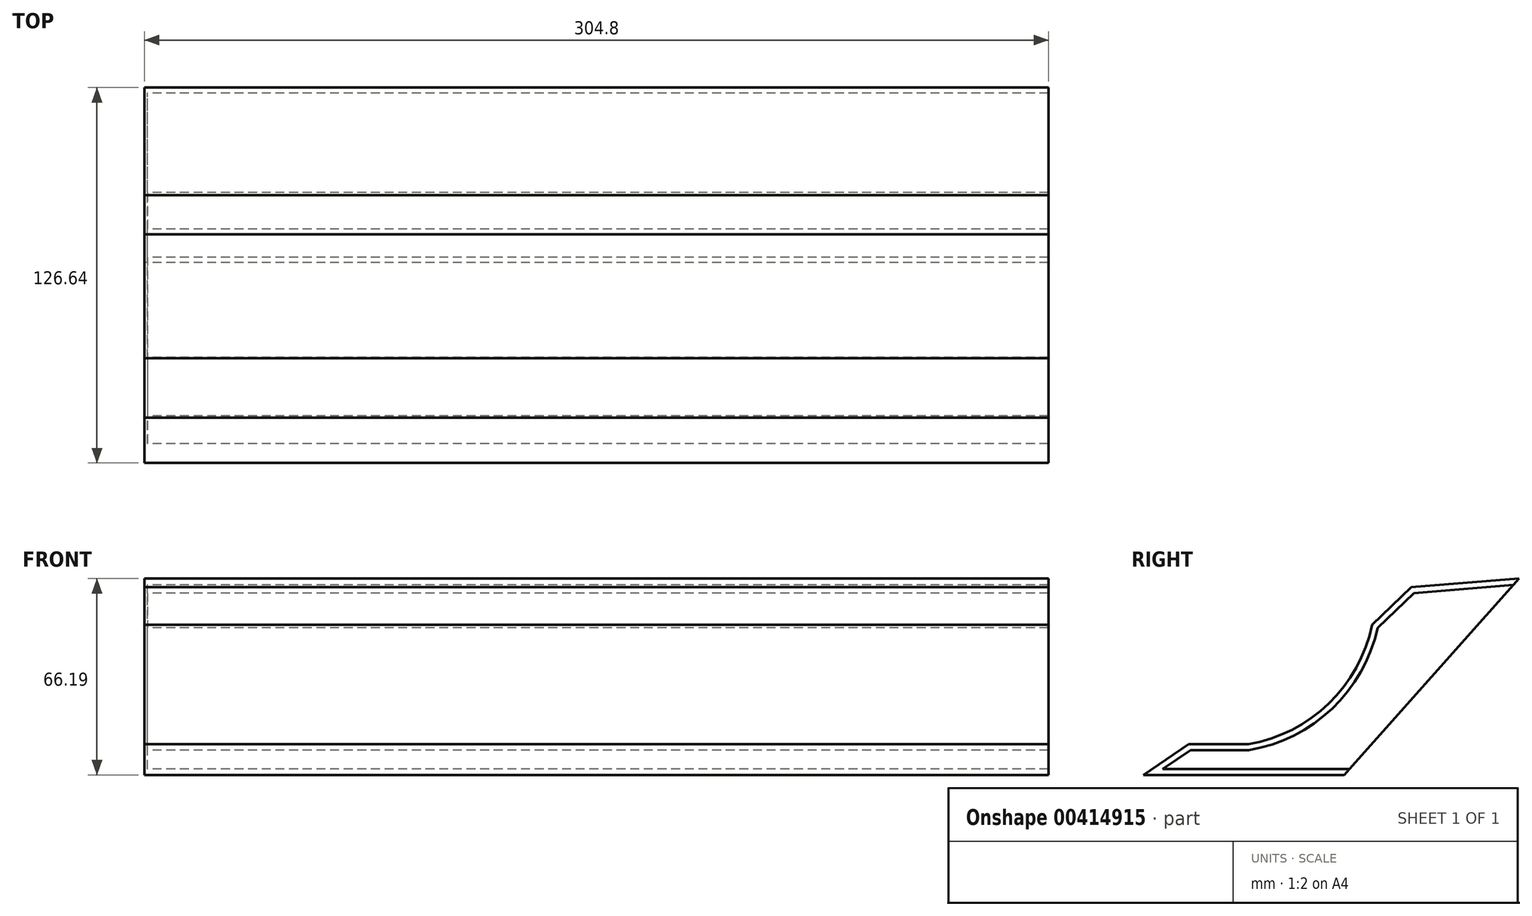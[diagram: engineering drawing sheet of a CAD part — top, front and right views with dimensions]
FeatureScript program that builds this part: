
annotation { "Feature Type Name" : "Feature", "Feature Type Description" : "" }
export const myFeature = defineFeature(function(context is Context, id is Id, definition is map)
    precondition{}
    {
        {
            var Q0;
            Q0=qCreatedBy(makeId("Right.planeOp"),FACE);
            var sketch = newSketch(context, id + "F0", { "sketchPlane" : qUnion([Q0])});
            skArc(sketch, "E0", {"start": v(-54.97, 0) * mm, "mid": v(-27.89, 13.7) * mm, "end": v(-13.24, 40.3) * mm});
            skLineSegment(sketch, "E1", {"start": v(-13.24, 40.3) * mm, "end": v(0, 52.93) * mm});
            skLineSegment(sketch, "E2", {"start": v(-22.72, -10.36) * mm, "end": v(36.26, 55.83) * mm});
            skLineSegment(sketch, "E3", {"start": v(-75.12, 0) * mm, "end": v(-54.97, 0) * mm});
            skLineSegment(sketch, "E4", {"start": v(36.26, 55.83) * mm, "end": v(0, 52.93) * mm});
            skLineSegment(sketch, "E5", {"start": v(-75.12, 0) * mm, "end": v(-90.38, -10.36) * mm});
            skPoint(sketch, "E6.orphan", {"position": v(-75.58, -10.36) * mm});
            skPoint(sketch, "E7.start.orphan", {"position": v(-77.31, -10.36) * mm});
            skLineSegment(sketch, "E8", {"start": v(-90.38, -10.36) * mm, "end": v(-22.72, -10.36) * mm});
            skSolve(sketch);
        }
        {
            var Q0;
            Q0=makeQuery(id+"F0.imprint","IMPRINT",FACE,{"disambiguationData":[TD([[makeQuery(id+"F0.imprint","IMPRINT",EDGE,{"derivedFrom":sQuery(id+"F0.wireOp",EDGE,"E0")}),-1.0]])]});
            extrude(context, id + "F1", {"entities" : qUnion([Q0]), "depth" : 1 * mm});
        }
        {
            var Q0;
            Q0=makeQuery(id+"F0.imprint","IMPRINT",FACE,{"disambiguationData":[TD([[makeQuery(id+"F0.imprint","IMPRINT",EDGE,{"derivedFrom":sQuery(id+"F0.wireOp",EDGE,"E0")}),-1.0]])]});
            var sketch = newSketch(context, id + "F2", { "sketchPlane" : qUnion([Q0])});
            skLineSegment(sketch, "E9.0", {"start": v(-74.5, -2) * mm, "end": v(-54.8, -2) * mm});
            skArc(sketch, "E9.1", {"start": v(-54.8, -2) * mm, "mid": v(-26.79, 12) * mm, "end": v(-11.41, 39.27) * mm});
            skLineSegment(sketch, "E9.2", {"start": v(-11.41, 39.27) * mm, "end": v(0.87, 51) * mm});
            skLineSegment(sketch, "E9.3", {"start": v(34.34, 53.67) * mm, "end": v(0.87, 51) * mm});
            skLineSegment(sketch, "E10.0", {"start": v(-83.87, -8.36) * mm, "end": v(-20.94, -8.36) * mm});
            skLineSegment(sketch, "E10.1", {"start": v(-74.5, -2) * mm, "end": v(-83.87, -8.36) * mm});
            skLineSegment(sketch, "E11.0", {"start": v(-90.38, -10.36) * mm, "end": v(-22.72, -10.36) * mm});
            skLineSegment(sketch, "E11.1", {"start": v(-75.12, 0) * mm, "end": v(-90.38, -10.36) * mm});
            skLineSegment(sketch, "E11.2", {"start": v(36.26, 55.83) * mm, "end": v(0, 52.93) * mm});
            skLineSegment(sketch, "E11.3", {"start": v(-13.24, 40.3) * mm, "end": v(0, 52.93) * mm});
            skArc(sketch, "E11.4", {"start": v(-54.97, 0) * mm, "mid": v(-27.89, 13.7) * mm, "end": v(-13.24, 40.3) * mm});
            skLineSegment(sketch, "E11.5", {"start": v(-75.12, 0) * mm, "end": v(-54.97, 0) * mm});
            skLineSegment(sketch, "E12", {"start": v(36.26, 55.83) * mm, "end": v(34.34, 53.67) * mm});
            skLineSegment(sketch, "E13.trimOffspring", {"start": v(-20.94, -8.36) * mm, "end": v(-22.72, -10.36) * mm});
            skSolve(sketch);
        }
        {
            var Q0;
            Q0 = qSketchRegion(id + "F2", true);
            extrude(context, id + "F3", {"entities" : qUnion([Q0]), "operationType" : NewBodyOperationType.ADD, "depth" : 304.8 * mm});
        }
    });
